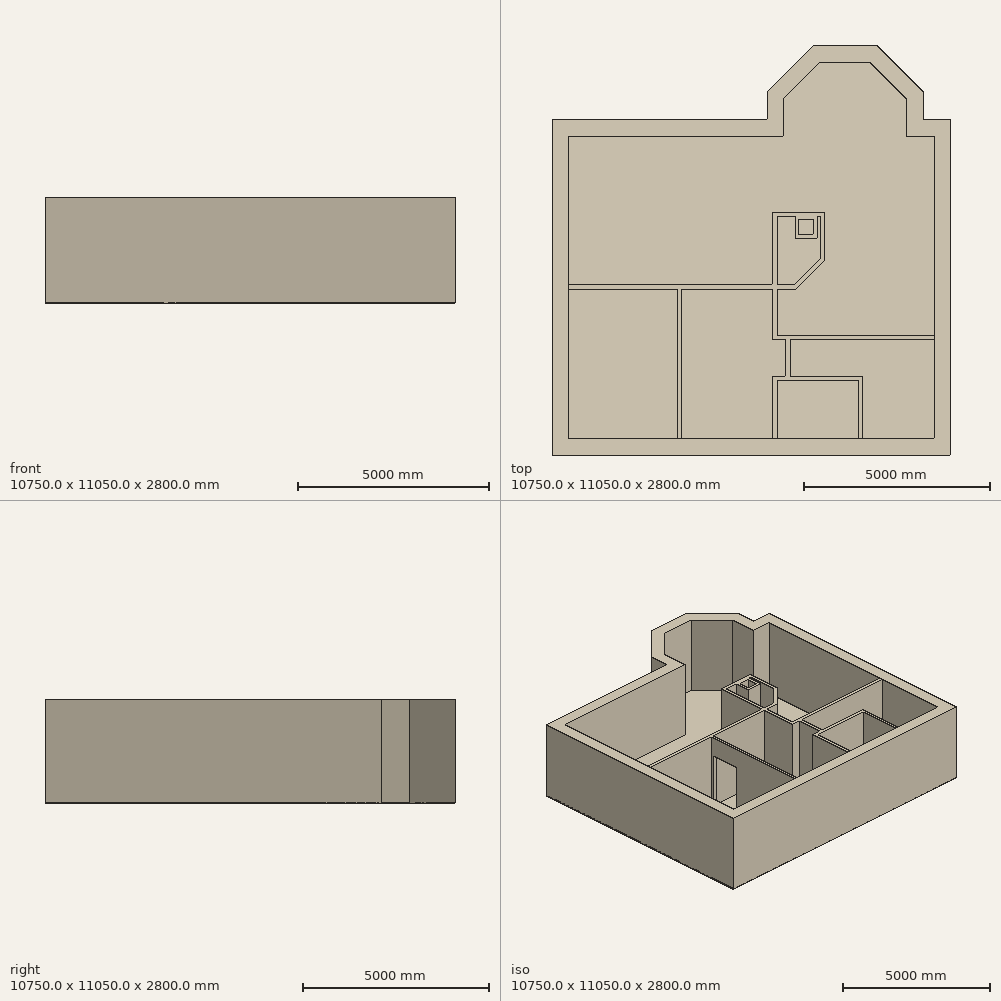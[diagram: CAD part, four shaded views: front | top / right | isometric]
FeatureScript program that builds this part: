
annotation { "Feature Type Name" : "Feature", "Feature Type Description" : "" }
export const myFeature = defineFeature(function(context is Context, id is Id, definition is map)
    precondition{}
    {
        {
            var Q0;
            Q0=qCreatedBy(makeId("Top.planeOp"),FACE);
            var sketch = newSketch(context, id + "F0", { "sketchPlane" : qUnion([Q0])});
            skLineSegment(sketch, "E0.bottom", {"start": v(5375, -4525) * mm, "end": v(-5375, -4525) * mm});
            skLineSegment(sketch, "E0.top", {"start": v(5375, 4525) * mm, "end": v(4625, 4525) * mm});
            skLineSegment(sketch, "E0.left", {"start": v(5375, -4525) * mm, "end": v(5375, 4525) * mm});
            skLineSegment(sketch, "E0.right", {"start": v(-5375, -4525) * mm, "end": v(-5375, 4525) * mm});
            skPoint(sketch, "E0.middle", {"position": v(0, 0) * mm});
            skLineSegment(sketch, "E1", {"start": v(425, 4525) * mm, "end": v(425, 5275) * mm});
            skLineSegment(sketch, "E2", {"start": v(425, 5275) * mm, "end": v(1675, 6525) * mm});
            skLineSegment(sketch, "E3", {"start": v(4625, 5275) * mm, "end": v(4625, 4525) * mm});
            skLineSegment(sketch, "E4", {"start": v(1675, 6525) * mm, "end": v(3375, 6525) * mm});
            skLineSegment(sketch, "E5", {"start": v(3375, 6525) * mm, "end": v(4625, 5275) * mm});
            skLineSegment(sketch, "E6.trimOffspring", {"start": v(425, 4525) * mm, "end": v(-5375, 4525) * mm});
            skLineSegment(sketch, "E7.0", {"start": v(875, 4075) * mm, "end": v(875, 5088.6) * mm});
            skLineSegment(sketch, "E7.1", {"start": v(875, 5088.6) * mm, "end": v(1861.4, 6075) * mm});
            skLineSegment(sketch, "E7.2", {"start": v(875, 4075) * mm, "end": v(-4925, 4075) * mm});
            skLineSegment(sketch, "E7.3", {"start": v(1861.4, 6075) * mm, "end": v(3188.6, 6075) * mm});
            skLineSegment(sketch, "E7.4", {"start": v(3188.6, 6075) * mm, "end": v(4175, 5088.6) * mm});
            skLineSegment(sketch, "E7.5", {"start": v(4175, 5088.6) * mm, "end": v(4175, 4075) * mm});
            skLineSegment(sketch, "E7.6", {"start": v(-4925, -4075) * mm, "end": v(-4925, 4075) * mm});
            skLineSegment(sketch, "E7.7", {"start": v(4925, -4075) * mm, "end": v(-4925, -4075) * mm});
            skLineSegment(sketch, "E7.8", {"start": v(4925, -4075) * mm, "end": v(4925, 4075) * mm});
            skLineSegment(sketch, "E7.9", {"start": v(4925, 4075) * mm, "end": v(4175, 4075) * mm});
            skPoint(sketch, "E8.endSnap0", {"position": v(4925, 0) * mm});
            skLineSegment(sketch, "E9", {"start": v(575, -4075) * mm, "end": v(575, -2390) * mm});
            skLineSegment(sketch, "E10", {"start": v(690, -1290) * mm, "end": v(4925, -1290) * mm});
            skLineSegment(sketch, "E11", {"start": v(575, -1290) * mm, "end": v(575, -40) * mm});
            skLineSegment(sketch, "E12", {"start": v(575, 2025) * mm, "end": v(4925, 2025) * mm});
            skLineSegment(sketch, "E13", {"start": v(2206.16, -1290) * mm, "end": v(2206.16, -590) * mm, "construction": true});
            skLineSegment(sketch, "E14", {"start": v(2206.16, -590) * mm, "end": v(4325, -590) * mm, "construction": true});
            skLineSegment(sketch, "E15", {"start": v(4325, -590) * mm, "end": v(4325, 998.03) * mm, "construction": true});
            skLineSegment(sketch, "E16", {"start": v(4325, 998.03) * mm, "end": v(3075, 998.03) * mm, "construction": true});
            skLineSegment(sketch, "E17", {"start": v(3075, 998.03) * mm, "end": v(3075, 2025) * mm, "construction": true});
            skLineSegment(sketch, "E18", {"start": v(1200.53, -40) * mm, "end": v(690, -40) * mm});
            skLineSegment(sketch, "E19", {"start": v(1200.53, -40) * mm, "end": v(1975, 734.47) * mm});
            skLineSegment(sketch, "E20", {"start": v(1975, 734.47) * mm, "end": v(1975, 2025) * mm});
            skLineSegment(sketch, "E21", {"start": v(575, -40) * mm, "end": v(575, -1290) * mm});
            skLineSegment(sketch, "E22.bottom", {"start": v(2067.96, 5092.97) * mm, "end": v(3067.96, 5092.97) * mm, "construction": true});
            skLineSegment(sketch, "E22.top", {"start": v(2067.96, 3092.97) * mm, "end": v(3067.96, 3092.97) * mm, "construction": true});
            skLineSegment(sketch, "E22.left", {"start": v(2067.96, 5092.97) * mm, "end": v(2067.96, 3092.97) * mm, "construction": true});
            skLineSegment(sketch, "E22.right", {"start": v(3067.96, 5092.97) * mm, "end": v(3067.96, 3092.97) * mm, "construction": true});
            skLineSegment(sketch, "E23.bottom", {"start": v(-975, -4075) * mm, "end": v(-1875, -4075) * mm, "construction": true});
            skLineSegment(sketch, "E23.top", {"start": v(-975, -775) * mm, "end": v(-1875, -775) * mm, "construction": true});
            skLineSegment(sketch, "E23.left", {"start": v(-975, -4075) * mm, "end": v(-975, -775) * mm, "construction": true});
            skLineSegment(sketch, "E23.right", {"start": v(-1875, -4075) * mm, "end": v(-1875, -775) * mm, "construction": true});
            skLineSegment(sketch, "E24", {"start": v(-1875, -4075) * mm, "end": v(-1875, -4075) * mm});
            skLineSegment(sketch, "E25", {"start": v(-1875, -4075) * mm, "end": v(-1875, -775) * mm});
            skLineSegment(sketch, "E26", {"start": v(-1875, 75) * mm, "end": v(575, 75) * mm});
            skLineSegment(sketch, "E27", {"start": v(-1875, 75) * mm, "end": v(-4925, 75) * mm});
            skLineSegment(sketch, "E28", {"start": v(-975, -3175) * mm, "end": v(-675, -3175) * mm, "construction": true});
            skLineSegment(sketch, "E29", {"start": v(-675, -3175) * mm, "end": v(-675, -4075) * mm, "construction": true});
            skLineSegment(sketch, "E30", {"start": v(575, -2390) * mm, "end": v(925, -2390) * mm});
            skLineSegment(sketch, "E31", {"start": v(3005, -2390) * mm, "end": v(3005, -4075) * mm});
            skLineSegment(sketch, "E32", {"start": v(-425, -2540) * mm, "end": v(575, -2540) * mm, "construction": true});
            skLineSegment(sketch, "E33", {"start": v(-1875, -40) * mm, "end": v(-1875, -775) * mm});
            skLineSegment(sketch, "E34.bottom", {"start": v(2854.25, -2533.29) * mm, "end": v(1954.25, -2533.29) * mm, "construction": true});
            skLineSegment(sketch, "E34.top", {"start": v(2854.25, -3433.29) * mm, "end": v(1954.25, -3433.29) * mm, "construction": true});
            skLineSegment(sketch, "E34.left", {"start": v(2854.25, -2533.29) * mm, "end": v(2854.25, -3433.29) * mm, "construction": true});
            skLineSegment(sketch, "E34.right", {"start": v(1954.25, -2533.29) * mm, "end": v(1954.25, -3433.29) * mm, "construction": true});
            skArc(sketch, "E35", {"start": v(-425, -2540) * mm, "mid": v(-132.1, -3247.1) * mm, "end": v(575, -3540) * mm, "construction": true});
            skLineSegment(sketch, "E36.bottom", {"start": v(928.73, -4075) * mm, "end": v(1478.73, -4075) * mm, "construction": true});
            skLineSegment(sketch, "E36.top", {"start": v(928.73, -3675) * mm, "end": v(1478.73, -3675) * mm, "construction": true});
            skLineSegment(sketch, "E36.left", {"start": v(928.73, -4075) * mm, "end": v(928.73, -3675) * mm, "construction": true});
            skLineSegment(sketch, "E36.right", {"start": v(1478.73, -4075) * mm, "end": v(1478.73, -3675) * mm, "construction": true});
            skLineSegment(sketch, "E37.bottom", {"start": v(1175, 1925) * mm, "end": v(1775, 1925) * mm, "construction": true});
            skLineSegment(sketch, "E37.top", {"start": v(1175, 1325) * mm, "end": v(1775, 1325) * mm, "construction": true});
            skLineSegment(sketch, "E37.left", {"start": v(1175, 1925) * mm, "end": v(1175, 1325) * mm, "construction": true});
            skLineSegment(sketch, "E37.right", {"start": v(1775, 1925) * mm, "end": v(1775, 1325) * mm, "construction": true});
            skLineSegment(sketch, "E38", {"start": v(1175, 1925) * mm, "end": v(1775, 1325) * mm, "construction": true});
            skLineSegment(sketch, "E39", {"start": v(1175, 1325) * mm, "end": v(1775, 1925) * mm, "construction": true});
            skPoint(sketch, "E40", {"position": v(1475, 1625) * mm});
            skPoint(sketch, "E41", {"position": v(575, -2390) * mm});
            skLineSegment(sketch, "E42", {"start": v(925, -2390) * mm, "end": v(925, -1405) * mm});
            skLineSegment(sketch, "E43", {"start": v(-4925, -40) * mm, "end": v(-1990, -40) * mm});
            skLineSegment(sketch, "E44", {"start": v(-1990, -40) * mm, "end": v(-1990, -4075) * mm});
            skLineSegment(sketch, "E45", {"start": v(-1875, -40) * mm, "end": v(575, -40) * mm});
            skLineSegment(sketch, "E46", {"start": v(690, -40) * mm, "end": v(690, -1290) * mm});
            skLineSegment(sketch, "E47", {"start": v(575, -1290) * mm, "end": v(575, -1405) * mm});
            skLineSegment(sketch, "E48", {"start": v(575, -1405) * mm, "end": v(925, -1405) * mm});
            skLineSegment(sketch, "E49", {"start": v(1040, -1405) * mm, "end": v(4925, -1405) * mm});
            skLineSegment(sketch, "E50", {"start": v(1040, -1405) * mm, "end": v(1040, -2390) * mm});
            skLineSegment(sketch, "E51", {"start": v(690, -4075) * mm, "end": v(690, -2505) * mm});
            skLineSegment(sketch, "E52", {"start": v(690, -2505) * mm, "end": v(2890, -2505) * mm});
            skLineSegment(sketch, "E53", {"start": v(2890, -2505) * mm, "end": v(2890, -4075) * mm});
            skLineSegment(sketch, "E54.trimOffspring", {"start": v(1040, -2390) * mm, "end": v(3005, -2390) * mm});
            skLineSegment(sketch, "E55", {"start": v(690, 75) * mm, "end": v(1152.9, 75) * mm});
            skLineSegment(sketch, "E56", {"start": v(1152.9, 75) * mm, "end": v(1860, 782.1) * mm});
            skLineSegment(sketch, "E57", {"start": v(1860, 782.1) * mm, "end": v(1860, 1910) * mm});
            skLineSegment(sketch, "E58", {"start": v(1860, 1910) * mm, "end": v(1775, 1910) * mm});
            skLineSegment(sketch, "E59", {"start": v(1175, 1910) * mm, "end": v(690, 1910) * mm});
            skLineSegment(sketch, "E60", {"start": v(690, 1910) * mm, "end": v(690, 75) * mm});
            skLineSegment(sketch, "E61.trimOffspring", {"start": v(575, 75) * mm, "end": v(575, 2025) * mm});
            skLineSegment(sketch, "E62", {"start": v(1175, 1910) * mm, "end": v(1175, 1325) * mm});
            skLineSegment(sketch, "E63", {"start": v(1775, 1325) * mm, "end": v(1775, 1910) * mm});
            skLineSegment(sketch, "E64", {"start": v(1175, 1325) * mm, "end": v(1775, 1325) * mm});
            skLineSegment(sketch, "E65.bottom", {"start": v(1675, 1425) * mm, "end": v(1275, 1425) * mm});
            skLineSegment(sketch, "E65.top", {"start": v(1675, 1825) * mm, "end": v(1275, 1825) * mm});
            skLineSegment(sketch, "E65.left", {"start": v(1675, 1425) * mm, "end": v(1675, 1825) * mm});
            skLineSegment(sketch, "E65.right", {"start": v(1275, 1425) * mm, "end": v(1275, 1825) * mm});
            skLineSegment(sketch, "E66.bottom", {"start": v(2086.4, 6525) * mm, "end": v(2956.4, 6525) * mm});
            skLineSegment(sketch, "E66.top", {"start": v(2086.4, 6075) * mm, "end": v(2956.4, 6075) * mm});
            skLineSegment(sketch, "E67.bottom", {"start": v(-4467.3, 4525) * mm, "end": v(-2737.3, 4525) * mm});
            skLineSegment(sketch, "E67.top", {"start": v(-4467.3, 4075) * mm, "end": v(-2737.3, 4075) * mm});
            skLineSegment(sketch, "E68.bottom", {"start": v(-1879.87, 4525) * mm, "end": v(-149.87, 4525) * mm});
            skLineSegment(sketch, "E68.top", {"start": v(-1879.87, 4075) * mm, "end": v(-149.87, 4075) * mm});
            skLineSegment(sketch, "E69", {"start": v(425, 5275) * mm, "end": v(875, 5088.6) * mm, "construction": true});
            skSolve(sketch);
        }
        {
            var Q0;
            Q0=makeQuery(id+"F0.imprint","IMPRINT",FACE,{"disambiguationData":[TD([[makeQuery(id+"F0.imprint","IMPRINT",EDGE,{"derivedFrom":sQuery(id+"F0.wireOp",EDGE,"E0.bottom")}),-1.0]])]});
            var Q1;
            Q1=makeQuery(id+"F0.imprint","IMPRINT",FACE,{"disambiguationData":[TD([[makeQuery(id+"F0.imprint","IMPRINT",EDGE,{"derivedFrom":sQuery(id+"F0.wireOp",EDGE,"E7.0")}),-1.0]])]});
            var Q2;
            Q2=makeQuery(id+"F0.imprint","IMPRINT",FACE,{"disambiguationData":[TD([[makeQuery(id+"F0.imprint","IMPRINT",EDGE,{"derivedFrom":sQuery(id+"F0.wireOp",EDGE,"E55")}),1.0]])]});
            var Q3;
            {var subQ4=sQuery(id+"F0.wireOp",EDGE,"E10");Q3=makeQuery(id+"F0.imprint","IMPRINT",FACE,{"disambiguationData":[TD([[makeQuery(id+"F0.imprint","IMPRINT",EDGE,{"derivedFrom":subQ4}),1.0]])]});}
            var Q4;
            {var subQ1=sQuery(id+"F0.wireOp",EDGE,"E9");Q4=makeQuery(id+"F0.imprint","IMPRINT",FACE,{"disambiguationData":[TD([[makeQuery(id+"F0.imprint","IMPRINT",EDGE,{"derivedFrom":subQ1}),1.0]])]});}
            var Q5;
            {var subQ3=sQuery(id+"F0.wireOp",EDGE,"E43");Q5=makeQuery(id+"F0.imprint","IMPRINT",FACE,{"disambiguationData":[TD([[makeQuery(id+"F0.imprint","IMPRINT",EDGE,{"derivedFrom":subQ3}),-1.0]])]});}
            var Q6;
            {var subQ0=sQuery(id+"F0.wireOp",EDGE,"E51");Q6=makeQuery(id+"F0.imprint","IMPRINT",FACE,{"disambiguationData":[TD([[makeQuery(id+"F0.imprint","IMPRINT",EDGE,{"derivedFrom":subQ0}),-1.0]])]});}
            var Q7;
            {var subQ4=sQuery(id+"F0.wireOp",EDGE,"E31");Q7=makeQuery(id+"F0.imprint","IMPRINT",FACE,{"disambiguationData":[TD([[makeQuery(id+"F0.imprint","IMPRINT",EDGE,{"derivedFrom":subQ4}),1.0]])]});}
            var Q8;
            Q8=makeQuery(id+"F0.imprint","IMPRINT",FACE,{"disambiguationData":[TD([[makeQuery(id+"F0.imprint","IMPRINT",EDGE,{"derivedFrom":sQuery(id+"F0.wireOp",EDGE,"E65.bottom")}),-1.0]])]});
            var Q9;
            {var subQ8=sQuery(id+"F0.wireOp",EDGE,"E9");Q9=makeQuery(id+"F0.imprint","IMPRINT",FACE,{"disambiguationData":[TD([[makeQuery(id+"F0.imprint","IMPRINT",EDGE,{"derivedFrom":subQ8}),-1.0]])]});}
            extrude(context, id + "F1", {"entities" : qUnion([Q0, Q1, Q2, Q3, Q4, Q5, Q6, Q7, Q8, Q9]), "depth" : 25 * mm, "offsetDistance" : 25 * mm});
        }
        {
            var Q0;
            Q0=makeQuery(id+"F0.imprint","IMPRINT",FACE,{"disambiguationData":[TD([[makeQuery(id+"F0.imprint","IMPRINT",EDGE,{"derivedFrom":sQuery(id+"F0.wireOp",EDGE,"E0.bottom")}),-1.0]])]});
            extrude(context, id + "F2", {"entities" : qUnion([Q0]), "depth" : 2800 * mm, "offsetDistance" : 25 * mm});
        }
        {
            var Q0;
            {var subQ8=sQuery(id+"F0.wireOp",EDGE,"E9");Q0=makeQuery(id+"F0.imprint","IMPRINT",FACE,{"disambiguationData":[TD([[makeQuery(id+"F0.imprint","IMPRINT",EDGE,{"derivedFrom":subQ8}),-1.0]])]});}
            var Q1;
            Q1=makeQuery(id+"F2.opExtrude","CAP_FACE",FACE,{"disambiguationData":[OSD([sQuery(id+"F0.wireOp",EDGE,"E0.bottom"),sQuery(id+"F0.wireOp",EDGE,"E0.top"),sQuery(id+"F0.wireOp",EDGE,"E0.left"),sQuery(id+"F0.wireOp",EDGE,"E0.right"),sQuery(id+"F0.wireOp",EDGE,"E1"),sQuery(id+"F0.wireOp",EDGE,"E2"),sQuery(id+"F0.wireOp",EDGE,"E3"),sQuery(id+"F0.wireOp",EDGE,"E4"),sQuery(id+"F0.wireOp",EDGE,"E5"),sQuery(id+"F0.wireOp",EDGE,"E6.trimOffspring"),sQuery(id+"F0.wireOp",EDGE,"E7.0"),sQuery(id+"F0.wireOp",EDGE,"E7.1"),sQuery(id+"F0.wireOp",EDGE,"E7.2"),sQuery(id+"F0.wireOp",EDGE,"E7.3"),sQuery(id+"F0.wireOp",EDGE,"E7.4"),sQuery(id+"F0.wireOp",EDGE,"E7.5"),sQuery(id+"F0.wireOp",EDGE,"E7.6"),sQuery(id+"F0.wireOp",EDGE,"E7.7"),sQuery(id+"F0.wireOp",EDGE,"E7.8"),sQuery(id+"F0.wireOp",EDGE,"E7.9")])],"isStart":false});
            extrude(context, id + "F3", {"entities" : qUnion([Q0]), "endBound" : BoundingType.UP_TO_SURFACE, "depth" : 25 * mm, "endBoundEntityFace" : qUnion([Q1]), "offsetDistance" : 25 * mm});
        }
        {
            var Q0;
            Q0=makeQuery(id+"F3.opExtrude","SWEPT_FACE",FACE,{"disambiguationData":[OSD([sQuery(id+"F0.wireOp",EDGE,"E44")])]});
            var sketch = newSketch(context, id + "F4", { "sketchPlane" : qUnion([Q0])});
            skLineSegment(sketch, "E70.bottom", {"start": v(165, 0) * mm, "end": v(1265, 0) * mm});
            skLineSegment(sketch, "E70.top", {"start": v(165, 2100) * mm, "end": v(1265, 2100) * mm});
            skLineSegment(sketch, "E70.left", {"start": v(165, 0) * mm, "end": v(165, 2100) * mm});
            skLineSegment(sketch, "E70.right", {"start": v(1265, 0) * mm, "end": v(1265, 2100) * mm});
            skSolve(sketch);
        }
        {
            var Q0;
            Q0=makeQuery(id+"F4.imprint","IMPRINT",FACE,{"disambiguationData":[TD([[makeQuery(id+"F4.imprint","IMPRINT",EDGE,{"derivedFrom":sQuery(id+"F4.wireOp",EDGE,"E70.bottom")}),1.0]])]});
            var Q1;
            Q1=makeQuery(id+"F3.opExtrude","SWEPT_FACE",FACE,{"disambiguationData":[OSD([sQuery(id+"F0.wireOp",EDGE,"E25"),sQuery(id+"F0.wireOp",EDGE,"E33")])]});
            extrude(context, id + "F5", {"entities" : qUnion([Q0]), "operationType" : NewBodyOperationType.REMOVE, "endBound" : BoundingType.UP_TO_SURFACE, "oppositeDirection" : true, "depth" : 25 * mm, "endBoundEntityFace" : qUnion([Q1]), "offsetDistance" : 25 * mm});
        }
    });
